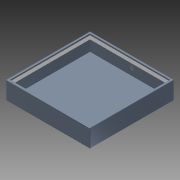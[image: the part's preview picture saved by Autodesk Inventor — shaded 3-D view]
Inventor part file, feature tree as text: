
AUTODESK INVENTOR PART (.ipt)
format: ipt  version: 2013 SP2 (Build 170200200, 200)  size: 182,784 bytes
history: native  units: in
note: dims shown in document units (in); Inventor stores cm internally (conversion verified against a paired STEP export)
features: extrude x10, sketch x7, projected_geometry x3, thread x2, plane x1, fillet x1, mirror x1
ambient origin geometry x8: Origin, YZ Plane, XZ Plane, XY Plane, X Axis, Y Axis, Z Axis, Center Point
bodies: Solid1 (feature_tree)
feature tree (25):
  extrude  "Extrusion1"  Depth=25.997in
  extrude  "Extrusion2"  Depth=0.0625in
  extrude  "Extrusion3"  Depth=5.375in TaperAngle=0.0deg
  plane  "Work Plane1"
  extrude  "Extrusion4"  [1 undecoded]
  fillet  "Fillet1"  Radius=0.0625in
  sketch  "Sketch5"  dims[d74=2.25in d75=1.315in]
  extrude  "Extrusion10"  Depth=1.315in
  extrude  "Extrusion5"  Depth=9.0in TaperAngle=0.0deg
  extrude  "Extrusion6"  Depth=1.0in
  extrude  "Extrusion7"  Depth=9.0in TaperAngle=0.0deg
  extrude  "Extrusion8"  Depth=0.794in TaperAngle=0.0deg
  thread  "Thread1"  [1 undecoded]
  thread  "Thread2"  [1 undecoded]
  extrude  "Extrusion9"  Depth=0.25in
  mirror  "Mirror1"
  sketch  "Sketch1"  dims[d0=25.997in d2=25.997in]
  sketch  "Sketch2"  dims[d5=0.0625in d6=0.0in d7=0.0625in]
  projected_geometry  "Projected Loop1"
  sketch  "Sketch3"  dims[d8=0.0625in d9=5.375in d10=0.0in]
  sketch  "Sketch4"  dims[d11=0.0625in d12=0.0in d13=-1.0in d16=0.0625in d17=0.0in]
  projected_geometry  "Projected Loop2"
  projected_geometry  "Projected Loop3"
  sketch  "Sketch6"  dims[d77=1.0in d78=0.0in d79=9.0in d80=0.0in]
  sketch  "Sketch7"  dims[d81=1.0625in d82=0.0in d83=1.0in d84=9.0in d85=0.0in d86=0.794in d87=0.0in d88=0.392in d89=0.0in d90=0.125in d91=0.25in d95=2.313in d96=0.625in d97=1.0in d98=0.0in d121=1.1875in d122=1.1875in d123=0.625in d124=0.625in d125=1.0in d126=0.0in]
note: 3 required parameter values undecoded (feature->parameter linkage not recoverable at this tier; creation-order binding heuristic only, values carry confidence <= 0.55)
